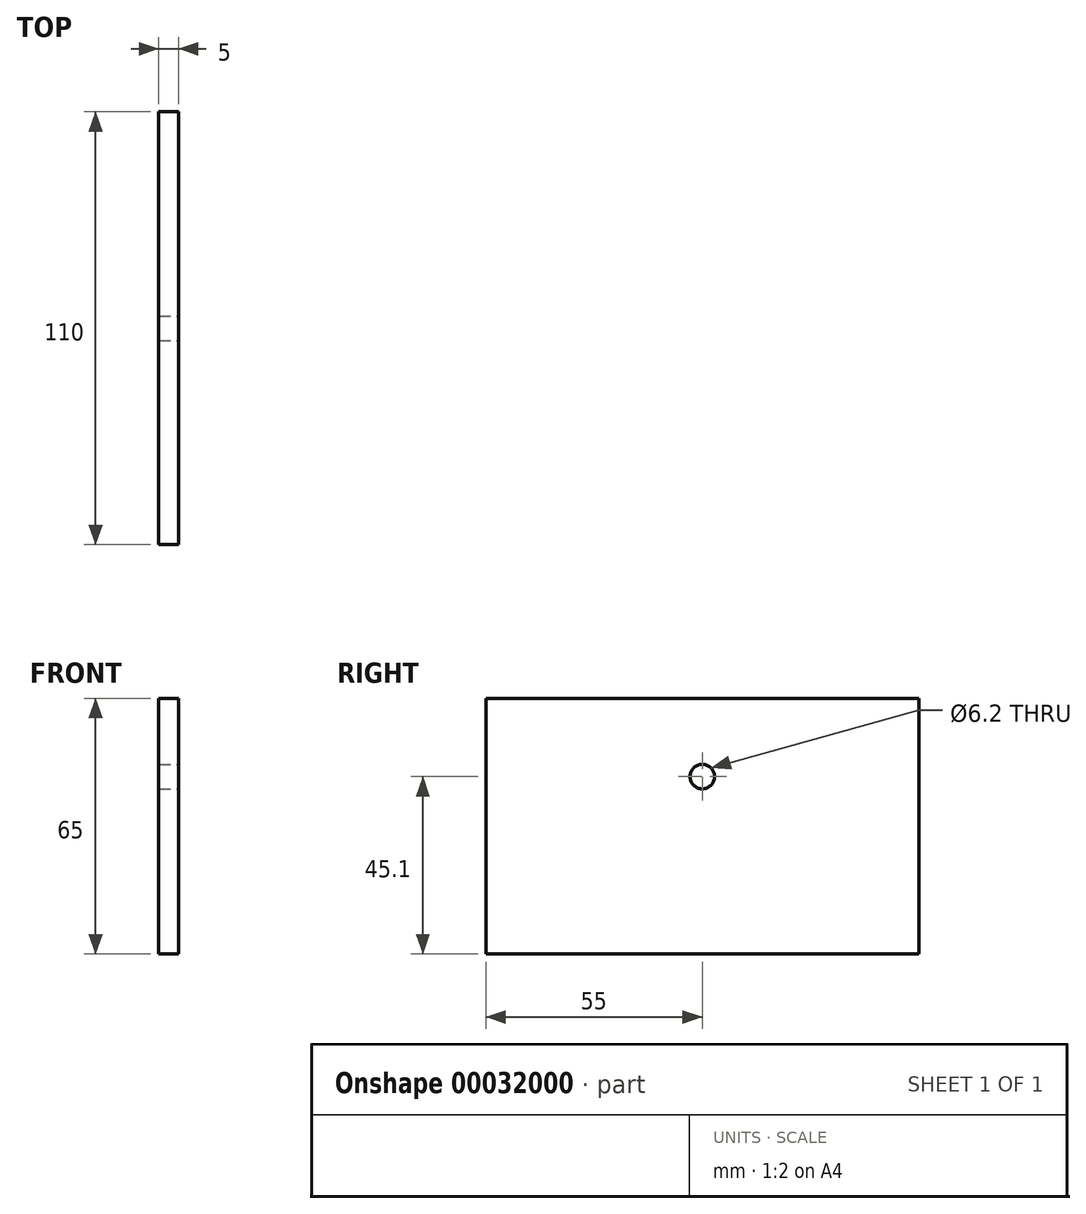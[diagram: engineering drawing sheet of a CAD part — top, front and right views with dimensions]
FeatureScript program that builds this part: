
annotation { "Feature Type Name" : "Feature", "Feature Type Description" : "" }
export const myFeature = defineFeature(function(context is Context, id is Id, definition is map)
    precondition{}
    {
        {
            var Q0;
            Q0=qCreatedBy(makeId("Right.planeOp"),FACE);
            var sketch = newSketch(context, id + "F0", { "sketchPlane" : qUnion([Q0])});
            skLineSegment(sketch, "E0.rect.bottom", {"start": v(55, -32.5) * mm, "end": v(-55, -32.5) * mm});
            skLineSegment(sketch, "E0.rect.top", {"start": v(55, 32.5) * mm, "end": v(-55, 32.5) * mm});
            skLineSegment(sketch, "E0.rect.left", {"start": v(55, -32.5) * mm, "end": v(55, 32.5) * mm});
            skLineSegment(sketch, "E0.rect.right", {"start": v(-55, -32.5) * mm, "end": v(-55, 32.5) * mm});
            skPoint(sketch, "E0.rect.middle", {"position": v(0, 0) * mm});
            skSolve(sketch);
        }
        {
            var Q0;
            Q0=makeQuery(id+"F0.imprint","IMPRINT",FACE,{"disambiguationData":[TD([[makeQuery(id+"F0.imprint","IMPRINT",EDGE,{"derivedFrom":sQuery(id+"F0.wireOp",EDGE,"E0.rect.bottom")}),-1.0]])]});
            extrude(context, id + "F1", {"entities" : qUnion([Q0]), "depth" : 5 * mm});
        }
        {
            var Q0;
            Q0=makeQuery(id+"F1.opExtrude","CAP_FACE",FACE,{"disambiguationData":[OSD([sQuery(id+"F0.wireOp",EDGE,"E0.rect.bottom"),sQuery(id+"F0.wireOp",EDGE,"E0.rect.top"),sQuery(id+"F0.wireOp",EDGE,"E0.rect.left"),sQuery(id+"F0.wireOp",EDGE,"E0.rect.right")])],"isStart":false});
            var sketch = newSketch(context, id + "F2", { "sketchPlane" : qUnion([Q0])});
            skCircle(sketch, "E1", {"center": v(0, 12.6) * mm, "radius": 3.1 * mm});
            skSolve(sketch);
        }
        {
            var Q0;
            Q0=makeQuery(id+"F2.imprint","IMPRINT",FACE,{"disambiguationData":[TD([[makeQuery(id+"F2.imprint","IMPRINT",EDGE,{"derivedFrom":sQuery(id+"F2.wireOp",EDGE,"E1")}),1.0]])]});
            extrude(context, id + "F3", {"entities" : qUnion([Q0]), "operationType" : NewBodyOperationType.REMOVE, "oppositeDirection" : true, "depth" : 25 * mm});
        }
    });
